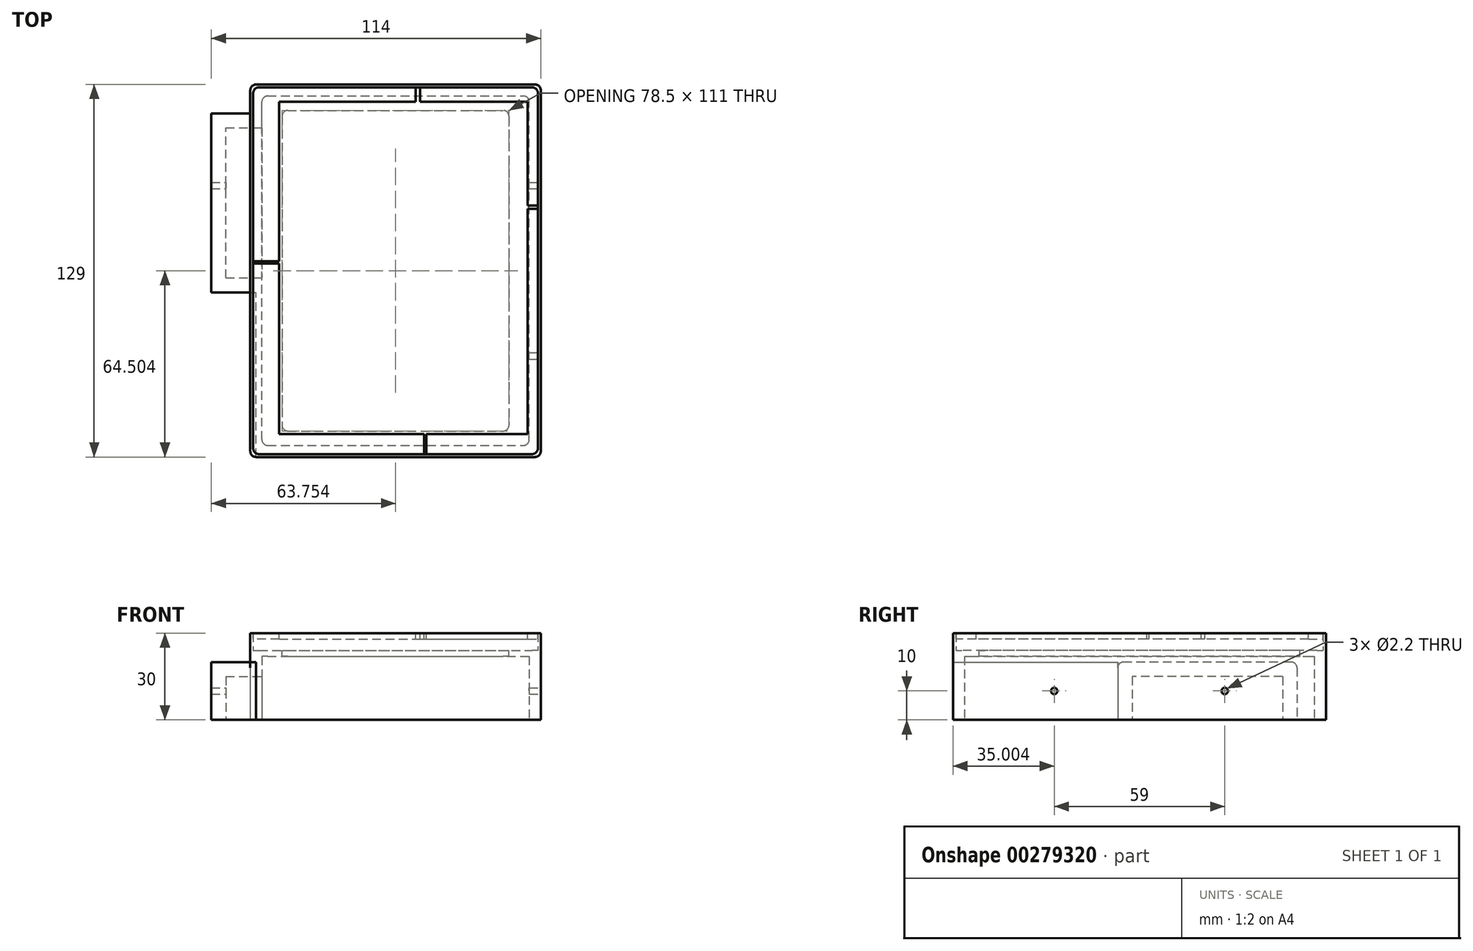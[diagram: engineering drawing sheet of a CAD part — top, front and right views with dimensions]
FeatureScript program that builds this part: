
annotation { "Feature Type Name" : "Feature", "Feature Type Description" : "" }
export const myFeature = defineFeature(function(context is Context, id is Id, definition is map)
    precondition{}
    {
        {
            var Q0;
            Q0=qCreatedBy(makeId("Top.planeOp"),FACE);
            var sketch = newSketch(context, id + "F0", { "sketchPlane" : qUnion([Q0])});
            skLineSegment(sketch, "E0.bottom", {"start": v(-48.46, 64.26) * mm, "end": v(46.04, 64.26) * mm});
            skLineSegment(sketch, "E0.top", {"start": v(-48.46, -62.74) * mm, "end": v(46.04, -62.74) * mm});
            skLineSegment(sketch, "E0.left", {"start": v(-50.46, 62.26) * mm, "end": v(-50.46, -60.74) * mm});
            skLineSegment(sketch, "E0.right", {"start": v(48.04, 62.26) * mm, "end": v(48.04, -60.74) * mm});
            skLineSegment(sketch, "E1.bottom", {"start": v(-49.46, 65.26) * mm, "end": v(47.04, 65.26) * mm});
            skLineSegment(sketch, "E1.top", {"start": v(-49.46, -63.74) * mm, "end": v(47.04, -63.74) * mm});
            skLineSegment(sketch, "E1.left", {"start": v(-51.46, 63.26) * mm, "end": v(-51.46, -61.74) * mm});
            skLineSegment(sketch, "E1.right", {"start": v(49.04, 63.26) * mm, "end": v(49.04, -61.74) * mm});
            skPoint(sketch, "E2.visualSharp", {"position": v(48.04, 64.26) * mm});
            skArc(sketch, "E2.filletArc", {"start": v(48.04, 62.26) * mm, "mid": v(47.46, 63.68) * mm, "end": v(46.04, 64.26) * mm});
            skPoint(sketch, "E3.visualSharp", {"position": v(49.04, 65.26) * mm});
            skArc(sketch, "E3.filletArc", {"start": v(49.04, 63.26) * mm, "mid": v(48.46, 64.68) * mm, "end": v(47.04, 65.26) * mm});
            skPoint(sketch, "E4.visualSharp", {"position": v(-50.46, 64.26) * mm});
            skArc(sketch, "E4.filletArc", {"start": v(-48.46, 64.26) * mm, "mid": v(-49.87, 63.68) * mm, "end": v(-50.46, 62.26) * mm});
            skPoint(sketch, "E5.visualSharp", {"position": v(-51.46, 65.26) * mm});
            skArc(sketch, "E5.filletArc", {"start": v(-49.46, 65.26) * mm, "mid": v(-50.87, 64.68) * mm, "end": v(-51.46, 63.26) * mm});
            skPoint(sketch, "E6.visualSharp", {"position": v(48.04, -62.74) * mm});
            skArc(sketch, "E6.filletArc", {"start": v(46.04, -62.74) * mm, "mid": v(47.46, -62.15) * mm, "end": v(48.04, -60.74) * mm});
            skPoint(sketch, "E7.visualSharp", {"position": v(49.04, -63.74) * mm});
            skArc(sketch, "E7.filletArc", {"start": v(47.04, -63.74) * mm, "mid": v(48.46, -63.15) * mm, "end": v(49.04, -61.74) * mm});
            skPoint(sketch, "E8.visualSharp", {"position": v(-50.46, -62.74) * mm});
            skArc(sketch, "E8.filletArc", {"start": v(-50.46, -60.74) * mm, "mid": v(-49.87, -62.15) * mm, "end": v(-48.46, -62.74) * mm});
            skPoint(sketch, "E9.visualSharp", {"position": v(-51.46, -63.74) * mm});
            skArc(sketch, "E9.filletArc", {"start": v(-51.46, -61.74) * mm, "mid": v(-50.87, -63.15) * mm, "end": v(-49.46, -63.74) * mm});
            skSolve(sketch);
        }
        {
            var Q0;
            Q0=qSketchRegion(id+"F0",true);
            extrude(context, id + "F1", {"entities" : qUnion([Q0]), "depth" : 6 * mm});
        }
        {
            var Q0;
            Q0=qCreatedBy(makeId("Top.planeOp"),FACE);
            var sketch = newSketch(context, id + "F2", { "sketchPlane" : qUnion([Q0])});
            skLineSegment(sketch, "E10.bottom", {"start": v(-49.46, 65.26) * mm, "end": v(47.04, 65.26) * mm});
            skLineSegment(sketch, "E10.top", {"start": v(-49.46, -63.74) * mm, "end": v(47.04, -63.74) * mm});
            skLineSegment(sketch, "E10.left", {"start": v(-51.46, 63.26) * mm, "end": v(-51.46, -61.74) * mm});
            skLineSegment(sketch, "E10.right", {"start": v(49.04, 63.26) * mm, "end": v(49.04, -61.74) * mm});
            skLineSegment(sketch, "E11.bottom", {"start": v(-38.46, 56.26) * mm, "end": v(36.04, 56.26) * mm});
            skLineSegment(sketch, "E11.top", {"start": v(-38.46, -54.74) * mm, "end": v(36.04, -54.74) * mm});
            skLineSegment(sketch, "E11.left", {"start": v(-40.46, 54.26) * mm, "end": v(-40.46, -52.74) * mm});
            skLineSegment(sketch, "E11.right", {"start": v(38.04, 54.26) * mm, "end": v(38.04, -52.74) * mm});
            skPoint(sketch, "E12.visualSharp", {"position": v(-40.46, -54.74) * mm});
            skArc(sketch, "E12.filletArc", {"start": v(-40.46, -52.74) * mm, "mid": v(-39.87, -54.15) * mm, "end": v(-38.46, -54.74) * mm});
            skPoint(sketch, "E13.visualSharp", {"position": v(38.04, -54.74) * mm});
            skArc(sketch, "E13.filletArc", {"start": v(36.04, -54.74) * mm, "mid": v(37.46, -54.15) * mm, "end": v(38.04, -52.74) * mm});
            skPoint(sketch, "E14.visualSharp", {"position": v(38.04, 56.26) * mm});
            skArc(sketch, "E14.filletArc", {"start": v(38.04, 54.26) * mm, "mid": v(37.46, 55.68) * mm, "end": v(36.04, 56.26) * mm});
            skPoint(sketch, "E15.visualSharp", {"position": v(-40.46, 56.26) * mm});
            skArc(sketch, "E15.filletArc", {"start": v(-38.46, 56.26) * mm, "mid": v(-39.87, 55.68) * mm, "end": v(-40.46, 54.26) * mm});
            skPoint(sketch, "E16.visualSharp", {"position": v(-51.46, -63.74) * mm});
            skArc(sketch, "E16.filletArc", {"start": v(-51.46, -61.74) * mm, "mid": v(-50.87, -63.15) * mm, "end": v(-49.46, -63.74) * mm});
            skPoint(sketch, "E17.visualSharp", {"position": v(49.04, -63.74) * mm});
            skArc(sketch, "E17.filletArc", {"start": v(47.04, -63.74) * mm, "mid": v(48.46, -63.15) * mm, "end": v(49.04, -61.74) * mm});
            skPoint(sketch, "E18.visualSharp", {"position": v(49.04, 65.26) * mm});
            skArc(sketch, "E18.filletArc", {"start": v(49.04, 63.26) * mm, "mid": v(48.46, 64.68) * mm, "end": v(47.04, 65.26) * mm});
            skPoint(sketch, "E19.visualSharp", {"position": v(-51.46, 65.26) * mm});
            skArc(sketch, "E19.filletArc", {"start": v(-49.46, 65.26) * mm, "mid": v(-50.87, 64.68) * mm, "end": v(-51.46, 63.26) * mm});
            skSolve(sketch);
        }
        {
            var Q0;
            Q0=qSketchRegion(id+"F2",true);
            extrude(context, id + "F3", {"entities" : qUnion([Q0]), "operationType" : NewBodyOperationType.ADD, "oppositeDirection" : true, "depth" : 2 * mm});
        }
        {
            var Q0;
            Q0=makeQuery(id+"F3.opExtrude","CAP_FACE",FACE,{"disambiguationData":[OSD([sQuery(id+"F2.wireOp",EDGE,"E10.bottom"),sQuery(id+"F2.wireOp",EDGE,"E10.top"),sQuery(id+"F2.wireOp",EDGE,"E10.left"),sQuery(id+"F2.wireOp",EDGE,"E10.right"),sQuery(id+"F2.wireOp",EDGE,"E11.bottom"),sQuery(id+"F2.wireOp",EDGE,"E11.top"),sQuery(id+"F2.wireOp",EDGE,"E11.left"),sQuery(id+"F2.wireOp",EDGE,"E11.right"),sQuery(id+"F2.wireOp",EDGE,"E12.filletArc"),sQuery(id+"F2.wireOp",EDGE,"E13.filletArc"),sQuery(id+"F2.wireOp",EDGE,"E14.filletArc"),sQuery(id+"F2.wireOp",EDGE,"E15.filletArc"),sQuery(id+"F2.wireOp",EDGE,"E16.filletArc"),sQuery(id+"F2.wireOp",EDGE,"E17.filletArc"),sQuery(id+"F2.wireOp",EDGE,"E18.filletArc"),sQuery(id+"F2.wireOp",EDGE,"E19.filletArc")])],"isStart":false});
            extrude(context, id + "F4", {"entities" : qUnion([Q0]), "operationType" : NewBodyOperationType.ADD, "depth" : 22 * mm});
        }
        {
            var Q0;
            Q0=makeQuery(id+"F4.opExtrude","CAP_FACE",FACE,{"disambiguationData":[OSD([sQuery(id+"F2.wireOp",EDGE,"E10.bottom"),sQuery(id+"F2.wireOp",EDGE,"E10.top"),sQuery(id+"F2.wireOp",EDGE,"E10.left"),sQuery(id+"F2.wireOp",EDGE,"E10.right"),sQuery(id+"F2.wireOp",EDGE,"E11.bottom"),sQuery(id+"F2.wireOp",EDGE,"E11.top"),sQuery(id+"F2.wireOp",EDGE,"E11.left"),sQuery(id+"F2.wireOp",EDGE,"E11.right"),sQuery(id+"F2.wireOp",EDGE,"E12.filletArc"),sQuery(id+"F2.wireOp",EDGE,"E13.filletArc"),sQuery(id+"F2.wireOp",EDGE,"E14.filletArc"),sQuery(id+"F2.wireOp",EDGE,"E15.filletArc"),sQuery(id+"F2.wireOp",EDGE,"E16.filletArc"),sQuery(id+"F2.wireOp",EDGE,"E17.filletArc"),sQuery(id+"F2.wireOp",EDGE,"E18.filletArc"),sQuery(id+"F2.wireOp",EDGE,"E19.filletArc")])],"isStart":false});
            var sketch = newSketch(context, id + "F5", { "sketchPlane" : qUnion([Q0])});
            skLineSegment(sketch, "E20.bottom", {"start": v(-45.46, 59.74) * mm, "end": v(43.04, 59.74) * mm});
            skLineSegment(sketch, "E20.top", {"start": v(-45.46, -61.26) * mm, "end": v(43.04, -61.26) * mm});
            skLineSegment(sketch, "E20.left", {"start": v(-47.46, 57.74) * mm, "end": v(-47.46, -59.26) * mm});
            skLineSegment(sketch, "E20.right", {"start": v(45.04, 57.74) * mm, "end": v(45.04, -59.26) * mm});
            skPoint(sketch, "E21.visualSharp", {"position": v(-47.46, 59.74) * mm});
            skArc(sketch, "E21.filletArc", {"start": v(-45.46, 59.74) * mm, "mid": v(-46.87, 59.15) * mm, "end": v(-47.46, 57.74) * mm});
            skPoint(sketch, "E22.visualSharp", {"position": v(45.04, 59.74) * mm});
            skArc(sketch, "E22.filletArc", {"start": v(45.04, 57.74) * mm, "mid": v(44.46, 59.15) * mm, "end": v(43.04, 59.74) * mm});
            skPoint(sketch, "E23.visualSharp", {"position": v(-47.46, -61.26) * mm});
            skArc(sketch, "E23.filletArc", {"start": v(-47.46, -59.26) * mm, "mid": v(-46.87, -60.68) * mm, "end": v(-45.46, -61.26) * mm});
            skPoint(sketch, "E24.visualSharp", {"position": v(45.04, -61.26) * mm});
            skArc(sketch, "E24.filletArc", {"start": v(43.04, -61.26) * mm, "mid": v(44.46, -60.68) * mm, "end": v(45.04, -59.26) * mm});
            skSolve(sketch);
        }
        {
            var Q0;
            Q0=qSketchRegion(id+"F5",true);
            extrude(context, id + "F6", {"entities" : qUnion([Q0]), "operationType" : NewBodyOperationType.REMOVE, "oppositeDirection" : true, "depth" : 22 * mm});
        }
        {
            var Q0;
            Q0=makeQuery(id+"F1.opExtrude","CAP_FACE",FACE,{"disambiguationData":[OSD([sQuery(id+"F0.wireOp",EDGE,"E0.bottom"),sQuery(id+"F0.wireOp",EDGE,"E0.top"),sQuery(id+"F0.wireOp",EDGE,"E0.left"),sQuery(id+"F0.wireOp",EDGE,"E0.right"),sQuery(id+"F0.wireOp",EDGE,"E1.bottom"),sQuery(id+"F0.wireOp",EDGE,"E1.top"),sQuery(id+"F0.wireOp",EDGE,"E1.left"),sQuery(id+"F0.wireOp",EDGE,"E1.right"),sQuery(id+"F0.wireOp",EDGE,"E2.filletArc"),sQuery(id+"F0.wireOp",EDGE,"E3.filletArc"),sQuery(id+"F0.wireOp",EDGE,"E4.filletArc"),sQuery(id+"F0.wireOp",EDGE,"E5.filletArc"),sQuery(id+"F0.wireOp",EDGE,"E6.filletArc"),sQuery(id+"F0.wireOp",EDGE,"E7.filletArc"),sQuery(id+"F0.wireOp",EDGE,"E8.filletArc"),sQuery(id+"F0.wireOp",EDGE,"E9.filletArc")])],"isStart":false});
            var sketch = newSketch(context, id + "F7", { "sketchPlane" : qUnion([Q0])});
            skLineSegment(sketch, "E25.bottom", {"start": v(-41.46, 59.26) * mm, "end": v(44.54, 59.26) * mm});
            skLineSegment(sketch, "E25.top", {"start": v(-41.46, -55.74) * mm, "end": v(44.54, -55.74) * mm});
            skLineSegment(sketch, "E25.left", {"start": v(-41.46, 59.26) * mm, "end": v(-41.46, -55.74) * mm});
            skLineSegment(sketch, "E25.right", {"start": v(44.54, 59.26) * mm, "end": v(44.54, -55.74) * mm});
            skLineSegment(sketch, "E26.bottom", {"start": v(5.73, 59.26) * mm, "end": v(7.27, 59.26) * mm});
            skLineSegment(sketch, "E26.top", {"start": v(5.73, 64.26) * mm, "end": v(7.27, 64.26) * mm});
            skLineSegment(sketch, "E26.left", {"start": v(7.27, 59.26) * mm, "end": v(7.27, 64.26) * mm});
            skLineSegment(sketch, "E26.right", {"start": v(5.73, 59.26) * mm, "end": v(5.73, 64.26) * mm});
            skLineSegment(sketch, "E27.bottom", {"start": v(-41.46, 4.07) * mm, "end": v(-50.46, 4.07) * mm});
            skLineSegment(sketch, "E27.top", {"start": v(-41.46, 3.27) * mm, "end": v(-50.46, 3.27) * mm});
            skLineSegment(sketch, "E27.left", {"start": v(-41.46, 4.07) * mm, "end": v(-41.46, 3.27) * mm});
            skLineSegment(sketch, "E27.right", {"start": v(-50.46, 4.07) * mm, "end": v(-50.46, 3.27) * mm});
            skLineSegment(sketch, "E28.bottom", {"start": v(8.66, -55.74) * mm, "end": v(9.49, -55.74) * mm});
            skLineSegment(sketch, "E28.top", {"start": v(8.66, -62.74) * mm, "end": v(9.49, -62.74) * mm});
            skLineSegment(sketch, "E28.left", {"start": v(8.66, -55.74) * mm, "end": v(8.66, -62.74) * mm});
            skLineSegment(sketch, "E28.right", {"start": v(9.49, -55.74) * mm, "end": v(9.49, -62.74) * mm});
            skLineSegment(sketch, "E29.bottom", {"start": v(44.54, 23.35) * mm, "end": v(48.04, 23.35) * mm});
            skLineSegment(sketch, "E29.top", {"start": v(44.54, 22.14) * mm, "end": v(48.04, 22.14) * mm});
            skLineSegment(sketch, "E29.left", {"start": v(44.54, 23.35) * mm, "end": v(44.54, 22.14) * mm});
            skLineSegment(sketch, "E29.right", {"start": v(48.04, 23.35) * mm, "end": v(48.04, 22.14) * mm});
            skSolve(sketch);
        }
        {
            var Q0;
            Q0=qSketchRegion(id+"F7",true);
            extrude(context, id + "F8", {"entities" : qUnion([Q0]), "oppositeDirection" : true, "depth" : 2 * mm});
        }
        {
            var Q0;
            {var subQ0=sQuery(id+"F2.wireOp",EDGE,"E10.left");Q0=makeQuery(id+"F4.boolean.opBoolean","MERGE",FACE,{"derivedFrom":[makeQuery(id+"F3.boolean.opBoolean","MERGE",FACE,{"derivedFrom":[makeQuery(id+"F1.opExtrude","SWEPT_FACE",FACE,{"disambiguationData":[OSD([sQuery(id+"F0.wireOp",EDGE,"E1.left")])]}),makeQuery(id+"F3.opExtrude","SWEPT_FACE",FACE,{"disambiguationData":[OSD([subQ0])]})]}),makeQuery(id+"F4.opExtrude","SWEPT_FACE",FACE,{"disambiguationData":[OSD([subQ0])]})]});}
            var sketch = newSketch(context, id + "F9", { "sketchPlane" : qUnion([Q0])});
            skLineSegment(sketch, "E30.bottom", {"start": v(-53.26, -4) * mm, "end": v(4.74, -4) * mm});
            skLineSegment(sketch, "E30.top", {"start": v(-55.26, -24) * mm, "end": v(6.74, -24) * mm});
            skLineSegment(sketch, "E30.left", {"start": v(-55.26, -6) * mm, "end": v(-55.26, -24) * mm});
            skLineSegment(sketch, "E30.right", {"start": v(6.74, -6) * mm, "end": v(6.74, -24) * mm});
            skPoint(sketch, "E31.visualSharp", {"position": v(-55.26, -4) * mm});
            skPoint(sketch, "E32.visualSharp", {"position": v(6.74, -4) * mm});
            skArc(sketch, "E33.filletArc", {"start": v(-53.26, -4) * mm, "mid": v(-54.68, -4.59) * mm, "end": v(-55.26, -6) * mm});
            skArc(sketch, "E34.filletArc", {"start": v(6.74, -6) * mm, "mid": v(6.15, -4.59) * mm, "end": v(4.74, -4) * mm});
            skSolve(sketch);
        }
        {
            var Q0;
            Q0=qSketchRegion(id+"F9",true);
            extrude(context, id + "F10", {"entities" : qUnion([Q0]), "operationType" : NewBodyOperationType.ADD, "depth" : 13.5 * mm});
        }
        {
            var Q0;
            Q0=makeQuery(id+"F10.boolean.opBoolean","MERGE",FACE,{"derivedFrom":[makeQuery(id+"F4.opExtrude","CAP_FACE",FACE,{"disambiguationData":[OSD([sQuery(id+"F2.wireOp",EDGE,"E10.bottom"),sQuery(id+"F2.wireOp",EDGE,"E10.top"),sQuery(id+"F2.wireOp",EDGE,"E10.left"),sQuery(id+"F2.wireOp",EDGE,"E10.right"),sQuery(id+"F2.wireOp",EDGE,"E11.bottom"),sQuery(id+"F2.wireOp",EDGE,"E11.top"),sQuery(id+"F2.wireOp",EDGE,"E11.left"),sQuery(id+"F2.wireOp",EDGE,"E11.right"),sQuery(id+"F2.wireOp",EDGE,"E12.filletArc"),sQuery(id+"F2.wireOp",EDGE,"E13.filletArc"),sQuery(id+"F2.wireOp",EDGE,"E14.filletArc"),sQuery(id+"F2.wireOp",EDGE,"E15.filletArc"),sQuery(id+"F2.wireOp",EDGE,"E16.filletArc"),sQuery(id+"F2.wireOp",EDGE,"E17.filletArc"),sQuery(id+"F2.wireOp",EDGE,"E18.filletArc"),sQuery(id+"F2.wireOp",EDGE,"E19.filletArc")])],"isStart":false}),makeQuery(id+"F10.opExtrude","SWEPT_FACE",FACE,{"disambiguationData":[OSD([sQuery(id+"F9.wireOp",EDGE,"E30.top")])]})]});
            var sketch = newSketch(context, id + "F11", { "sketchPlane" : qUnion([Q0])});
            skLineSegment(sketch, "E35.bottom", {"start": v(-79, 66.77) * mm, "end": v(-49.46, 66.77) * mm});
            skLineSegment(sketch, "E35.top", {"start": v(-79, 6.74) * mm, "end": v(-49.46, 6.74) * mm});
            skLineSegment(sketch, "E35.left", {"start": v(-79, 66.77) * mm, "end": v(-79, 6.74) * mm});
            skLineSegment(sketch, "E35.right", {"start": v(-49.46, 66.77) * mm, "end": v(-49.46, 6.74) * mm});
            skSolve(sketch);
        }
        {
            var Q0;
            Q0=qSketchRegion(id+"F11",true);
            extrude(context, id + "F12", {"entities" : qUnion([Q0]), "operationType" : NewBodyOperationType.REMOVE, "oppositeDirection" : true, "depth" : 20 * mm});
        }
        {
            var Q0;
            Q0=makeQuery(id+"F10.boolean.opBoolean","MERGE",FACE,{"derivedFrom":[makeQuery(id+"F4.opExtrude","CAP_FACE",FACE,{"disambiguationData":[OSD([sQuery(id+"F2.wireOp",EDGE,"E10.bottom"),sQuery(id+"F2.wireOp",EDGE,"E10.top"),sQuery(id+"F2.wireOp",EDGE,"E10.left"),sQuery(id+"F2.wireOp",EDGE,"E10.right"),sQuery(id+"F2.wireOp",EDGE,"E11.bottom"),sQuery(id+"F2.wireOp",EDGE,"E11.top"),sQuery(id+"F2.wireOp",EDGE,"E11.left"),sQuery(id+"F2.wireOp",EDGE,"E11.right"),sQuery(id+"F2.wireOp",EDGE,"E12.filletArc"),sQuery(id+"F2.wireOp",EDGE,"E13.filletArc"),sQuery(id+"F2.wireOp",EDGE,"E14.filletArc"),sQuery(id+"F2.wireOp",EDGE,"E15.filletArc"),sQuery(id+"F2.wireOp",EDGE,"E16.filletArc"),sQuery(id+"F2.wireOp",EDGE,"E17.filletArc"),sQuery(id+"F2.wireOp",EDGE,"E18.filletArc"),sQuery(id+"F2.wireOp",EDGE,"E19.filletArc")])],"isStart":false}),makeQuery(id+"F10.opExtrude","SWEPT_FACE",FACE,{"disambiguationData":[OSD([sQuery(id+"F9.wireOp",EDGE,"E30.top")])]})]});
            var sketch = newSketch(context, id + "F13", { "sketchPlane" : qUnion([Q0])});
            skLineSegment(sketch, "E36.bottom", {"start": v(-59.96, 1.74) * mm, "end": v(-35.72, 1.74) * mm});
            skLineSegment(sketch, "E36.top", {"start": v(-59.96, -50.26) * mm, "end": v(-35.72, -50.26) * mm});
            skLineSegment(sketch, "E36.left", {"start": v(-59.96, 1.74) * mm, "end": v(-59.96, -50.26) * mm});
            skLineSegment(sketch, "E36.right", {"start": v(-35.72, 1.74) * mm, "end": v(-35.72, -50.26) * mm});
            skSolve(sketch);
        }
        {
            var Q0;
            Q0=qSketchRegion(id+"F13",true);
            extrude(context, id + "F14", {"entities" : qUnion([Q0]), "operationType" : NewBodyOperationType.REMOVE, "oppositeDirection" : true, "depth" : 15 * mm});
        }
        {
            var Q0;
            {var subQ0=sQuery(id+"F2.wireOp",EDGE,"E10.right");Q0=makeQuery(id+"F4.boolean.opBoolean","MERGE",FACE,{"derivedFrom":[makeQuery(id+"F3.boolean.opBoolean","MERGE",FACE,{"derivedFrom":[makeQuery(id+"F1.opExtrude","SWEPT_FACE",FACE,{"disambiguationData":[OSD([sQuery(id+"F0.wireOp",EDGE,"E1.right")])]}),makeQuery(id+"F3.opExtrude","SWEPT_FACE",FACE,{"disambiguationData":[OSD([subQ0])]})]}),makeQuery(id+"F4.opExtrude","SWEPT_FACE",FACE,{"disambiguationData":[OSD([subQ0])]})]});}
            var sketch = newSketch(context, id + "F15", { "sketchPlane" : qUnion([Q0])});
            skCircle(sketch, "E37", {"center": v(30.26, -14) * mm, "radius": 1.1 * mm});
            skSolve(sketch);
        }
        {
            var Q0;
            {var subQ0=sQuery(id+"F2.wireOp",EDGE,"E10.right");Q0=makeQuery(id+"F4.boolean.opBoolean","MERGE",FACE,{"derivedFrom":[makeQuery(id+"F3.boolean.opBoolean","MERGE",FACE,{"derivedFrom":[makeQuery(id+"F1.opExtrude","SWEPT_FACE",FACE,{"disambiguationData":[OSD([sQuery(id+"F0.wireOp",EDGE,"E1.right")])]}),makeQuery(id+"F3.opExtrude","SWEPT_FACE",FACE,{"disambiguationData":[OSD([subQ0])]})]}),makeQuery(id+"F4.opExtrude","SWEPT_FACE",FACE,{"disambiguationData":[OSD([subQ0])]})]});}
            var sketch = newSketch(context, id + "F16", { "sketchPlane" : qUnion([Q0])});
            skCircle(sketch, "E38", {"center": v(-28.74, -14) * mm, "radius": 1.1 * mm});
            skSolve(sketch);
        }
        {
            var Q0;
            Q0=qSketchRegion(id+"F15",true);
            extrude(context, id + "F17", {"entities" : qUnion([Q0]), "operationType" : NewBodyOperationType.REMOVE, "oppositeDirection" : true, "depth" : 120 * mm});
        }
        {
            var Q0;
            Q0=qSketchRegion(id+"F16",true);
            extrude(context, id + "F18", {"entities" : qUnion([Q0]), "operationType" : NewBodyOperationType.REMOVE, "oppositeDirection" : true, "depth" : 25 * mm});
        }
    });
